# Revit family: Haworth_Masters_Desk_CredenzawithLateralFiles
name_source: partatom
category: Furniture Systems
revit_build: Autodesk Revit 2018 (Build: 20170223_1515(x64)
units: mm (PartAtom-declared; Revit-internal decimal feet)

## family parameters
Always vertical = Yes
Cut with Voids When Loaded = No
OmniClass Number = 23.40.70.14.64.21
OmniClass Title = Systems Furniture
Part Type = Normal
Room Calculation Point = No
Round Connector Dimension = Use Diameter
Shared = No
Work Plane-Based = No

## types (2) — shared parameters
Actual Depth = 24"
Actual Height = 29 1/8"
Assembly Code = E2020200
Bar Pull = Yes
Classic Pull = No
Finger Pull = No
Linear Pull = No
Manufacturer = Haworth
Model = XZZ
Pedestal Depth = 23"
Revision Number = 1
Size = Verify Final Dim. w/ Haworth
Sustainability Info = https://www.haworth.com
Thickness = 1 3/16"
URL = www.haworth.com
URL - Product = http://www.haworth.com
Warranty = http://www.haworth.com

## per-type parameters (varying)
| type | Actual Grommet | Actual Width | Description | Lateral File Width | With Grommet | With Kneespace |
| XZZM-2490 - 30" Wide Lateral - With Kneespace | Yes | 90" | Haworth - Masters - Credenza with 30" Wide Lateral Files | 30" | Yes | Yes |
| XZZL-2472 - 36" Wide Lateral - Without Kneespace | No | 72" | Haworth - Masters - Credenza with 36" Wide Lateral Files | 36" | No | No |

## geometry (parser evidence)
native form markers: Sweep x13
no freeform markers — native parametric forms only
